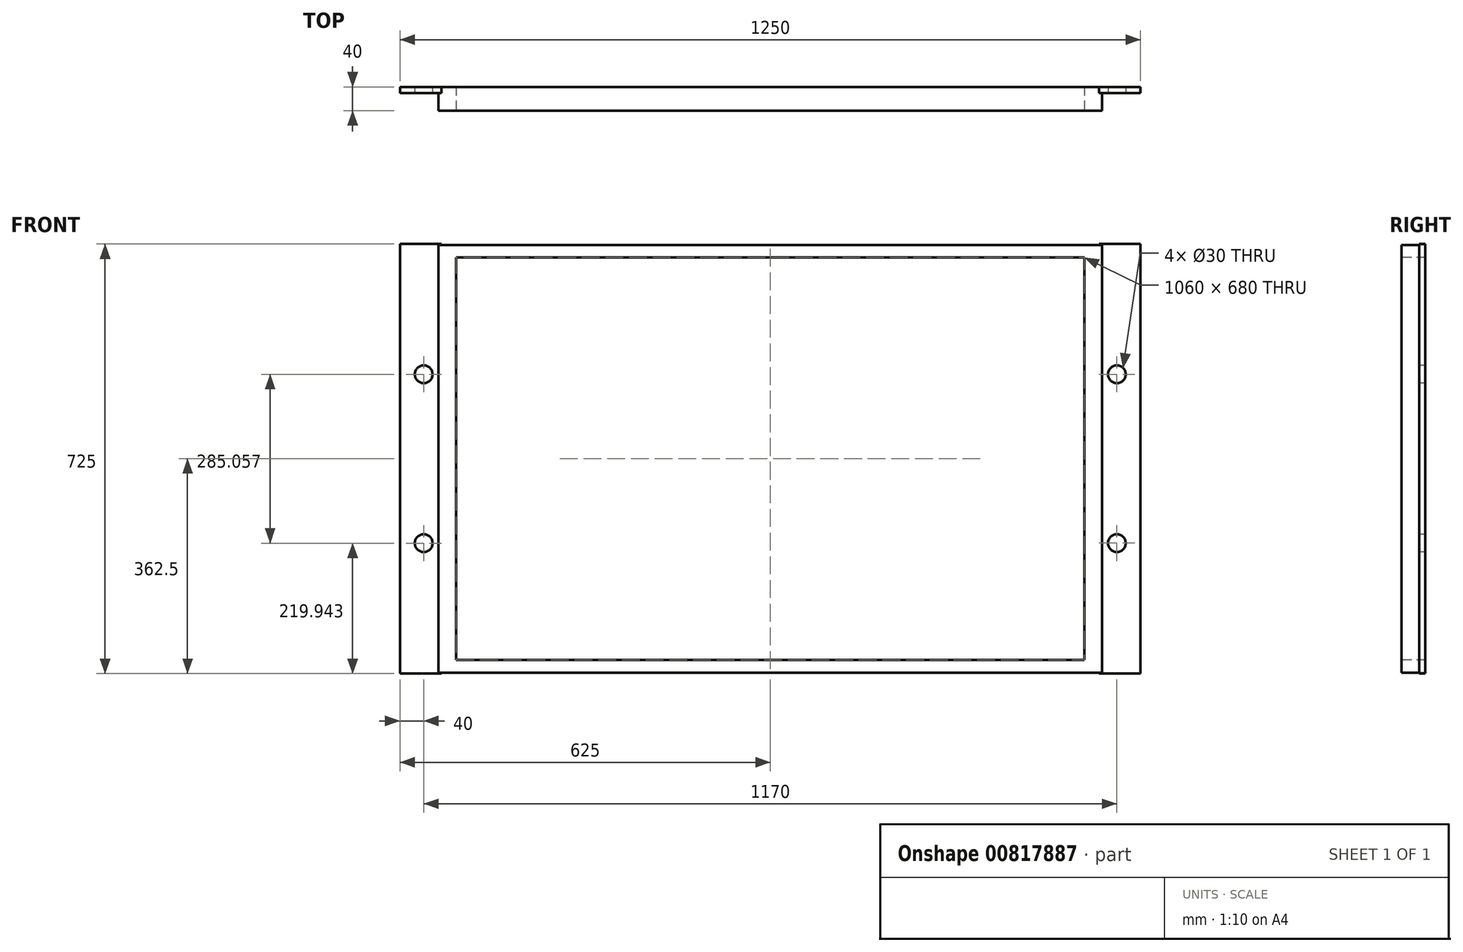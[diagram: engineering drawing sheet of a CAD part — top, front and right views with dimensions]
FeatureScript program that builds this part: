
annotation { "Feature Type Name" : "Feature", "Feature Type Description" : "" }
export const myFeature = defineFeature(function(context is Context, id is Id, definition is map)
    precondition{}
    {
        {
            var Q0;
            Q0=qCreatedBy(makeId("Front.planeOp"),FACE);
            var sketch = newSketch(context, id + "F0", { "sketchPlane" : qUnion([Q0])});
            skLineSegment(sketch, "E0.bottom", {"start": v(560, 361) * mm, "end": v(-560, 361) * mm});
            skLineSegment(sketch, "E0.top", {"start": v(560, -361) * mm, "end": v(-560, -361) * mm});
            skLineSegment(sketch, "E0.left", {"start": v(560, 361) * mm, "end": v(560, -361) * mm});
            skLineSegment(sketch, "E0.right", {"start": v(-560, 361) * mm, "end": v(-560, -361) * mm});
            skPoint(sketch, "E0.middle", {"position": v(0, 0) * mm});
            skSolve(sketch);
        }
        {
            var Q0;
            Q0=makeQuery(id+"F0.imprint","IMPRINT",FACE,{"disambiguationData":[TD([[makeQuery(id+"F0.imprint","IMPRINT",EDGE,{"derivedFrom":sQuery(id+"F0.wireOp",EDGE,"E0.bottom")}),1.0]])]});
            extrude(context, id + "F1", {"entities" : qUnion([Q0]), "depth" : 40 * mm, "offsetDistance" : 25.4 * mm});
        }
        {
            var Q0;
            Q0=qCreatedBy(makeId("Front.planeOp"),FACE);
            var sketch = newSketch(context, id + "F2", { "sketchPlane" : qUnion([Q0])});
            skLineSegment(sketch, "E1.bottom", {"start": v(625, 362.5) * mm, "end": v(555, 362.5) * mm});
            skLineSegment(sketch, "E1.top", {"start": v(625, -362.5) * mm, "end": v(555, -362.5) * mm});
            skLineSegment(sketch, "E1.left", {"start": v(625, 362.5) * mm, "end": v(625, -362.5) * mm});
            skLineSegment(sketch, "E1.right", {"start": v(555, 362.5) * mm, "end": v(555, -362.5) * mm});
            skPoint(sketch, "E1.middle", {"position": v(590, 0) * mm});
            skSolve(sketch);
        }
        {
            var Q0;
            Q0 = qSketchRegion(id + "F2", true);
            extrude(context, id + "F3", {"entities" : qUnion([Q0]), "operationType" : NewBodyOperationType.ADD, "depth" : 10 * mm, "offsetDistance" : 25.4 * mm});
        }
        {
            var Q0;
            Q0=makeQuery(id+"F3.opExtrude","CAP_FACE",FACE,{"disambiguationData":[OSD([sQuery(id+"F2.wireOp",EDGE,"E1.bottom"),sQuery(id+"F2.wireOp",EDGE,"E1.top"),sQuery(id+"F2.wireOp",EDGE,"E1.left"),sQuery(id+"F2.wireOp",EDGE,"E1.right")])],"isStart":false});
            var sketch = newSketch(context, id + "F4", { "sketchPlane" : qUnion([Q0])});
            skCircle(sketch, "E2", {"center": v(585, 142.5) * mm, "radius": 15 * mm});
            skSolve(sketch);
        }
        {
            var Q0;
            Q0=sQuery(id+"F4.wireOp",VERTEX,"E2.center");
            var Q1;
            Q1=makeQuery(id+"F1.opExtrude","SWEPT_BODY",BODY,{"disambiguationData":[OSD([sQuery(id+"F0.wireOp",EDGE,"E0.bottom"),sQuery(id+"F0.wireOp",EDGE,"E0.top"),sQuery(id+"F0.wireOp",EDGE,"E0.left"),sQuery(id+"F0.wireOp",EDGE,"E0.right")])]});
            hole(context, id + "F5", {"style" : HoleStyle.SIMPLE, "endStyle" : HoleEndStyle.THROUGH, "holeDiameter" : 30 * mm, "majorDiameter" : 6.35 * mm, "isTappedThrough" : true, "tappedDepth" : 12.7 * mm, "tapClearance" : 3, "locations" : qUnion([Q0]), "scope" : qUnion([Q1])});
        }
        {
            var Q0;
            Q0=makeQuery(id+"F3.opExtrude","CAP_FACE",FACE,{"disambiguationData":[OSD([sQuery(id+"F2.wireOp",EDGE,"E1.bottom"),sQuery(id+"F2.wireOp",EDGE,"E1.top"),sQuery(id+"F2.wireOp",EDGE,"E1.left"),sQuery(id+"F2.wireOp",EDGE,"E1.right")])],"isStart":false});
            var sketch = newSketch(context, id + "F6", { "sketchPlane" : qUnion([Q0])});
            skCircle(sketch, "E3", {"center": v(585, -142.5) * mm, "radius": 15 * mm});
            skSolve(sketch);
        }
        {
            var Q0;
            Q0=sQuery(id+"F6.wireOp",VERTEX,"E3.center");
            var Q1;
            Q1=makeQuery(id+"F1.opExtrude","SWEPT_BODY",BODY,{"disambiguationData":[OSD([sQuery(id+"F0.wireOp",EDGE,"E0.bottom"),sQuery(id+"F0.wireOp",EDGE,"E0.top"),sQuery(id+"F0.wireOp",EDGE,"E0.left"),sQuery(id+"F0.wireOp",EDGE,"E0.right")])]});
            hole(context, id + "F7", {"style" : HoleStyle.SIMPLE, "endStyle" : HoleEndStyle.THROUGH, "holeDiameter" : 30 * mm, "majorDiameter" : 6.35 * mm, "isTappedThrough" : true, "tappedDepth" : 12.7 * mm, "tapClearance" : 3, "locations" : qUnion([Q0]), "scope" : qUnion([Q1])});
        }
        {
            var Q0;
            Q0=qCreatedBy(makeId("Front.planeOp"),FACE);
            var sketch = newSketch(context, id + "F8", { "sketchPlane" : qUnion([Q0])});
            skLineSegment(sketch, "E4.bottom", {"start": v(-555, 362.5) * mm, "end": v(-625, 362.5) * mm});
            skLineSegment(sketch, "E4.top", {"start": v(-555, -362.5) * mm, "end": v(-625, -362.5) * mm});
            skLineSegment(sketch, "E4.left", {"start": v(-555, 362.5) * mm, "end": v(-555, -362.5) * mm});
            skLineSegment(sketch, "E4.right", {"start": v(-625, 362.5) * mm, "end": v(-625, -362.5) * mm});
            skPoint(sketch, "E4.middle", {"position": v(-590, 0) * mm});
            skSolve(sketch);
        }
        {
            var Q0;
            Q0=makeQuery(id+"F8.imprint","IMPRINT",FACE,{"disambiguationData":[TD([[makeQuery(id+"F8.imprint","IMPRINT",EDGE,{"derivedFrom":sQuery(id+"F8.wireOp",EDGE,"E4.bottom")}),1.0]])]});
            extrude(context, id + "F9", {"entities" : qUnion([Q0]), "operationType" : NewBodyOperationType.ADD, "depth" : 10 * mm, "offsetDistance" : 25.4 * mm});
        }
        {
            var Q0;
            Q0=makeQuery(id+"F9.opExtrude","CAP_FACE",FACE,{"disambiguationData":[OSD([sQuery(id+"F8.wireOp",EDGE,"E4.bottom"),sQuery(id+"F8.wireOp",EDGE,"E4.top"),sQuery(id+"F8.wireOp",EDGE,"E4.left"),sQuery(id+"F8.wireOp",EDGE,"E4.right")])],"isStart":false});
            var sketch = newSketch(context, id + "F10", { "sketchPlane" : qUnion([Q0])});
            skCircle(sketch, "E5", {"center": v(-585, 142.5) * mm, "radius": 15 * mm});
            skCircle(sketch, "E6", {"center": v(-585, -142.56) * mm, "radius": 15 * mm});
            skSolve(sketch);
        }
        {
            var Q0;
            Q0=sQuery(id+"F10.wireOp",VERTEX,"E5.center");
            var Q1;
            Q1=sQuery(id+"F10.wireOp",VERTEX,"E6.center");
            var Q2;
            Q2=makeQuery(id+"F1.opExtrude","SWEPT_BODY",BODY,{"disambiguationData":[OSD([sQuery(id+"F0.wireOp",EDGE,"E0.bottom"),sQuery(id+"F0.wireOp",EDGE,"E0.top"),sQuery(id+"F0.wireOp",EDGE,"E0.left"),sQuery(id+"F0.wireOp",EDGE,"E0.right")])]});
            hole(context, id + "F11", {"style" : HoleStyle.SIMPLE, "endStyle" : HoleEndStyle.THROUGH, "holeDiameter" : 30 * mm, "majorDiameter" : 6.35 * mm, "isTappedThrough" : true, "tappedDepth" : 12.7 * mm, "tapClearance" : 3, "locations" : qUnion([Q0, Q1]), "scope" : qUnion([Q2])});
        }
        {
            var Q0;
            Q0=makeQuery(id+"F1.opExtrude","CAP_FACE",FACE,{"disambiguationData":[OSD([sQuery(id+"F0.wireOp",EDGE,"E0.bottom"),sQuery(id+"F0.wireOp",EDGE,"E0.top"),sQuery(id+"F0.wireOp",EDGE,"E0.left"),sQuery(id+"F0.wireOp",EDGE,"E0.right")])],"isStart":false});
            var sketch = newSketch(context, id + "F12", { "sketchPlane" : qUnion([Q0])});
            skLineSegment(sketch, "E7.bottom", {"start": v(530, 340) * mm, "end": v(-530, 340) * mm});
            skLineSegment(sketch, "E7.top", {"start": v(530, -340) * mm, "end": v(-530, -340) * mm});
            skLineSegment(sketch, "E7.left", {"start": v(530, 340) * mm, "end": v(530, -340) * mm});
            skLineSegment(sketch, "E7.right", {"start": v(-530, 340) * mm, "end": v(-530, -340) * mm});
            skPoint(sketch, "E7.middle", {"position": v(0, 0) * mm});
            skSolve(sketch);
        }
        {
            var Q0;
            Q0=makeQuery(id+"F12.imprint","IMPRINT",FACE,{"disambiguationData":[TD([[makeQuery(id+"F12.imprint","IMPRINT",EDGE,{"derivedFrom":sQuery(id+"F12.wireOp",EDGE,"E7.bottom")}),1.0]])]});
            extrude(context, id + "F13", {"entities" : qUnion([Q0]), "operationType" : NewBodyOperationType.REMOVE, "endBound" : BoundingType.THROUGH_ALL, "oppositeDirection" : true, "depth" : 25.4 * mm, "offsetDistance" : 25.4 * mm});
        }
    });
